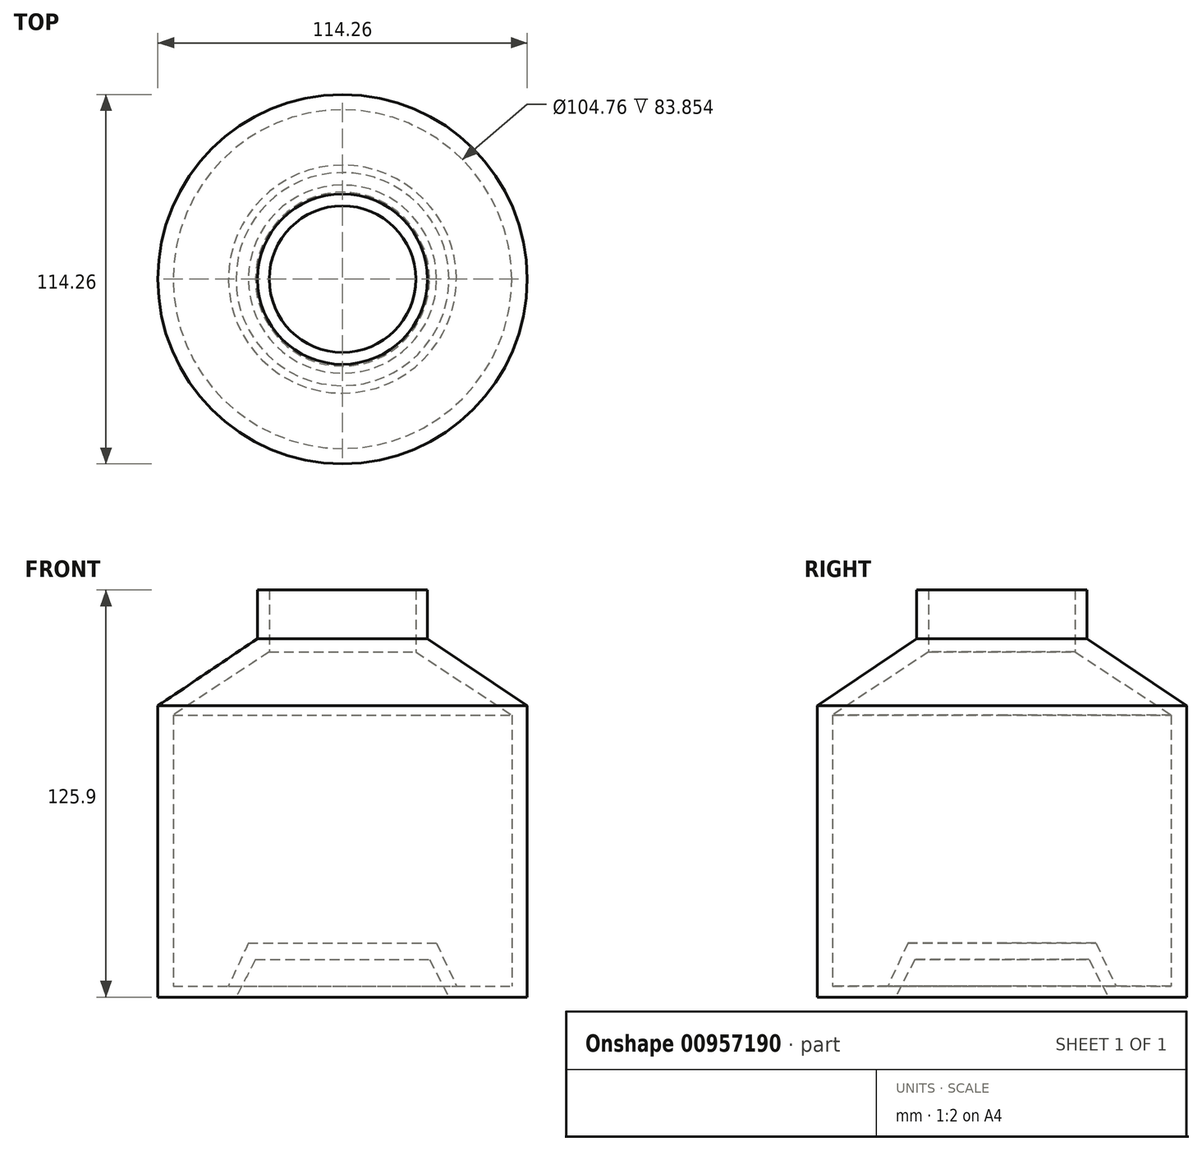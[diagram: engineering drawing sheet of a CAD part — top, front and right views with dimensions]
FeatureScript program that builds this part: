
annotation { "Feature Type Name" : "Feature", "Feature Type Description" : "" }
export const myFeature = defineFeature(function(context is Context, id is Id, definition is map)
    precondition{}
    {
        {
            var Q0;
            Q0=qCreatedBy(makeId("Front.planeOp"),FACE);
            var sketch = newSketch(context, id + "F0", { "sketchPlane" : qUnion([Q0])});
            skLineSegment(sketch, "E0", {"start": v(0, 0) * mm, "end": v(0, 74.97) * mm, "construction": true});
            skSolve(sketch);
        }
        {
            var Q0;
            Q0=qCreatedBy(makeId("Front.planeOp"),FACE);
            var sketch = newSketch(context, id + "F1", { "sketchPlane" : qUnion([Q0])});
            skLineSegment(sketch, "E1", {"start": v(0, 0) * mm, "end": v(26.9, 0) * mm});
            skLineSegment(sketch, "E2", {"start": v(26.9, 0) * mm, "end": v(32.95, -11.66) * mm});
            skLineSegment(sketch, "E3", {"start": v(32.95, -11.66) * mm, "end": v(57.13, -11.66) * mm});
            skLineSegment(sketch, "E4", {"start": v(57.13, -11.66) * mm, "end": v(57.13, 78.43) * mm});
            skLineSegment(sketch, "E5", {"start": v(57.13, 78.43) * mm, "end": v(26.33, 99.19) * mm});
            skLineSegment(sketch, "E6", {"start": v(26.33, 99.19) * mm, "end": v(26.33, 114.24) * mm});
            skLineSegment(sketch, "E7", {"start": v(26.33, 114.24) * mm, "end": v(22.67, 114.24) * mm});
            skLineSegment(sketch, "E8", {"start": v(22.67, 114.24) * mm, "end": v(22.67, 95.11) * mm});
            skLineSegment(sketch, "E9", {"start": v(22.67, 95.11) * mm, "end": v(52.38, 75.58) * mm});
            skLineSegment(sketch, "E10", {"start": v(52.38, 75.58) * mm, "end": v(52.38, -8.28) * mm});
            skLineSegment(sketch, "E11", {"start": v(52.38, -8.28) * mm, "end": v(35.27, -8.28) * mm});
            skLineSegment(sketch, "E12", {"start": v(35.27, -8.28) * mm, "end": v(29.1, 5.07) * mm});
            skLineSegment(sketch, "E13", {"start": v(29.1, 5.07) * mm, "end": v(0, 5.07) * mm});
            skLineSegment(sketch, "E14", {"start": v(0, 5.07) * mm, "end": v(0, 0) * mm});
            skSolve(sketch);
        }
        {
            var Q0;
            Q0 = qSketchRegion(id + "F1", true);
            var Q1;
            Q1=sQuery(id+"F0.wireOp",EDGE,"E0");
            revolve(context, id + "F2", {"surfaceOperationType" : NewSurfaceOperationType.NEW, "entities" : qUnion([Q0]), "axis" : qUnion([Q1]), "revolveType" : RevolveType.FULL});
        }
    });
